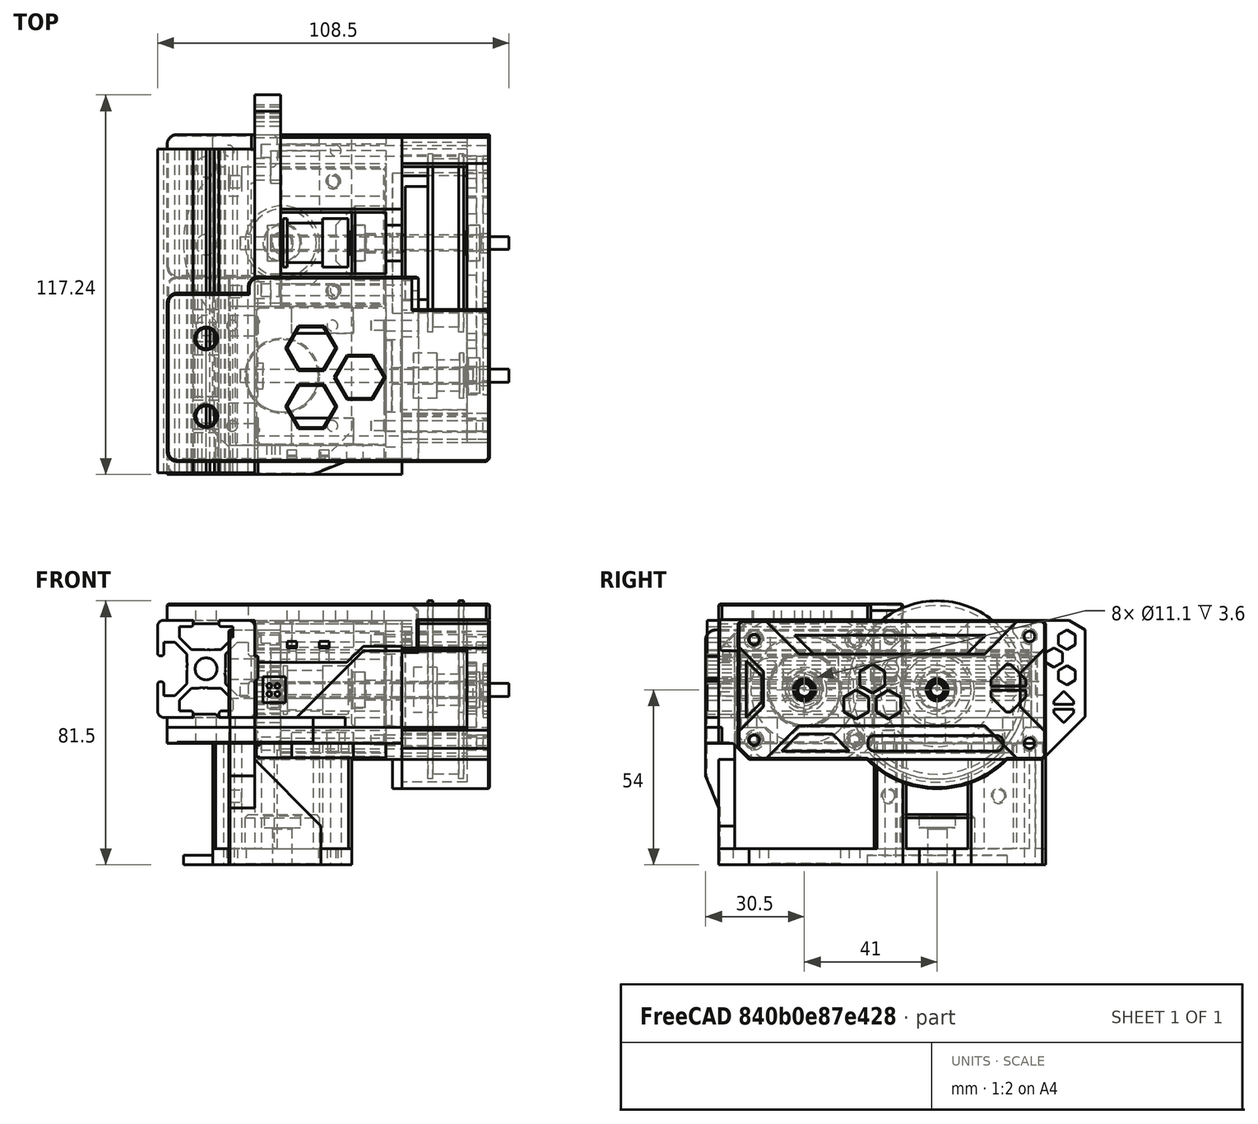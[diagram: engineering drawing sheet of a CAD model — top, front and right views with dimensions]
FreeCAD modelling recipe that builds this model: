
FCSTD DOCUMENT  (FreeCAD 0.19R24291 (Git))
Label: 80t-gearbox
License: Other
LicenseURL: GPL3
objects: Part::Box×56, Part::Chamfer×48, Part::Cylinder×46, Part::MultiFuse×43, Part::Cut×30, Part::Feature×25, Part::Fillet×5, Part::Refine×3, Part::MultiCommon×1
note: 257 computed .brp shape members not serialized (recipe doc carries the construction recipe); baked Part::Feature solids carry a one-line shape summary decoded from their .brp

FEATURE [Part::Feature] Cut001002  label="80t-pulley"
  Placement = pos=(64.5,41,8.5) rot=(0.707107,0,-0.707107;3.14159rad)
  shape: bbox 18 x 55 x 55 mm, 10 faces (baked)
FEATURE [Part::Feature] Cut001001  label="16t-pulley"
  Placement = pos=(64.5,0,8.5) rot=(0,-1,0;1.5708rad)
  shape: bbox 15.5 x 13.9 x 13.9 mm, 8 faces (baked)
FEATURE [Part::Feature] Fusion006002011004053036004001001  label="motor-40mm"
  Placement = pos=(0.5,0,8.5) rot=(0,1,0;1.5708rad)
  shape: bbox 67 x 47 x 42 mm, 100 faces (baked)
FEATURE [Part::Feature] Extrude001003002002002002  label="Extrude001003002002004"
  Placement = pos=(-15,-30,15) rot=(-1,0,0;1.5708rad)
  shape: bbox 30 x 100 x 30 mm, 95 faces (baked)
FEATURE [Part::Feature] Cut001  label="20t-pulley"
  Placement = pos=(8.8,41,8.5) rot=(0.707107,0,0.707107;3.14159rad)
  shape: bbox 20 x 15 x 15 mm, 8 faces (baked)
FEATURE [Part::Feature] Cut001003  label="MR115ZZ001"
  Placement = pos=(69.5,0,8.5) rot=(0,-1,0;1.5708rad)
  shape: bbox 4 x 11 x 11 mm, 4 faces (baked)
FEATURE [Part::Feature] Cut001004  label="MR115ZZ002"
  Placement = pos=(69.5,41,8.5) rot=(0,-1,0;1.5708rad)
  shape: bbox 4 x 11 x 11 mm, 4 faces (baked)
FEATURE [Part::Feature] Cut001005  label="MR115ZZ003"
  Placement = pos=(34,41,8.5) rot=(0,-1,0;1.5708rad)
  shape: bbox 4 x 11 x 11 mm, 4 faces (baked)
FEATURE [Part::Cylinder] Cylinder  label="POSA"
  Angle = 360
  AttacherType = Attacher::AttachEngine3D
  Height = 83
  Placement = pos=(-4.5,0,8.5) rot=(0,1,0;1.5708rad)
  Radius = 2
FEATURE [Part::Cylinder] Cylinder001  label="POSB"
  Angle = 360
  AttacherType = Attacher::AttachEngine3D
  Height = 83
  Placement = pos=(-4.5,41,8.5) rot=(0,1,0;1.5708rad)
  Radius = 2
FEATURE [Part::Box] Box  label="Cube"
  AttacherType = Attacher::AttachEngine3D
  Height = 43
  Length = 5
  Placement = pos=(40.5,-26.5,-13) rot=(0,0,1;0rad)
  Width = 101
FEATURE [Part::Box] Box001  label="Cube001"
  AttacherType = Attacher::AttachEngine3D
  Height = 43
  Length = 8
  Placement = pos=(0,21.5,-13) rot=(0,0,1;0rad)
  Width = 53
FEATURE [Part::Cylinder] Cylinder002  label="br01"
  Angle = 360
  AttacherType = Attacher::AttachEngine3D
  Height = 4
  Placement = pos=(4,41,8.5) rot=(0,1,0;1.5708rad)
  Radius = 5.55
FEATURE [Part::Cylinder] Cylinder003  label="br002"
  Angle = 360
  AttacherType = Attacher::AttachEngine3D
  Height = 4
  Placement = pos=(30,41,8.5) rot=(0,1,0;1.5708rad)
  Radius = 5.55
FEATURE [Part::Cylinder] Cylinder004  label="br003"
  Angle = 360
  AttacherType = Attacher::AttachEngine3D
  Height = 4
  Placement = pos=(65.5,41,8.5) rot=(0,1,0;1.5708rad)
  Radius = 5.55
FEATURE [Part::Cylinder] Cylinder005  label="br004"
  Angle = 360
  AttacherType = Attacher::AttachEngine3D
  Height = 4
  Placement = pos=(65.5,0,8.5) rot=(0,1,0;1.5708rad)
  Radius = 5.55
FEATURE [Part::Box] Box002  label="Cube002"
  AttacherType = Attacher::AttachEngine3D
  Height = 8
  Length = 27
  Placement = pos=(-27,30.5,-8) rot=(0,0,1;0rad)
  Width = 44
FEATURE [Part::Box] Box003  label="Cube003"
  AttacherType = Attacher::AttachEngine3D
  Height = 7.8
  Length = 1
  Placement = pos=(-1,29.5,11.1) rot=(0,0,1;0rad)
  Width = 32
FEATURE [Part::Feature] Cut001006  label="MR115ZZ004"
  Placement = pos=(8,41,8.5) rot=(0,-1,0;1.5708rad)
  shape: bbox 4 x 11 x 11 mm, 4 faces (baked)
FEATURE [Part::Cut] Cut
  Base = -> Box001
  Tool = -> Cylinder002
FEATURE [Part::Chamfer] Chamfer
  Base = -> Cut
  Edges = 1 edges r=0.4: [Edge13]
FEATURE [Part::Cylinder] Cylinder006  label="Cylinder"
  Angle = 360
  AttacherType = Attacher::AttachEngine3D
  Height = 10
  Placement = pos=(-3e-15,26.5,15) rot=(0,1,0;1.5708rad)
  Radius = 2.65
FEATURE [Part::Cylinder] Cylinder007  label="Cylinder001"
  Angle = 360
  AttacherType = Attacher::AttachEngine3D
  Height = 3
  Placement = pos=(5,26.5,15) rot=(0,1,0;1.5708rad)
  Radius = 5
FEATURE [Part::MultiFuse] Fusion
  Shapes = -> [Cylinder007,Cylinder006]
FEATURE [Part::Feature] Fusion006002011004053036004001002  label="Fusion001"
  Placement = pos=(0,38,0) rot=(0,0,1;0rad)
  shape: bbox 10 x 10 x 10 mm, 7 faces (baked)
FEATURE [Part::MultiFuse] Fusion006002011004053036004001003
  Shapes = -> [Fusion,Fusion006002011004053036004001002]
FEATURE [Part::Box] Box004  label="Cube004"
  AttacherType = Attacher::AttachEngine3D
  Height = 10
  Length = 3
  Placement = pos=(5,16.5,10) rot=(0,0,1;0rad)
  Width = 10
FEATURE [Part::MultiFuse] Fusion006002011004053036004001004
  Shapes = -> [Box004,Fusion006002011004053036004001003]
FEATURE [Part::Cut] Cut001007
  Base = -> Chamfer
  Tool = -> Fusion006002011004053036004001004
FEATURE [Part::Box] Box005  label="Cube005"
  AttacherType = Attacher::AttachEngine3D
  Height = 7.8
  Length = 1
  Placement = pos=(-1,67.5,11.1) rot=(0,0,1;0rad)
  Width = 7
FEATURE [Part::Box] Box006  label="Cube006"
  AttacherType = Attacher::AttachEngine3D
  Height = 13
  Length = 10
  Placement = pos=(-1.5,20.5,-13) rot=(0,0,1;0rad)
  Width = 10
FEATURE [Part::Cut] Cut001008
  Base = -> Cut001007
  Tool = -> Box006
FEATURE [Part::Chamfer] Chamfer001
  Base = -> Cut001008
  Edges = 1 edges r=5: [Edge30]
FEATURE [Part::Fillet] Fillet
  Base = -> Box002
  Edges = 2 edges r=3: [Edge1,Edge3]
FEATURE [Part::Box] Box007  label="Cube007"
  AttacherType = Attacher::AttachEngine3D
  Height = 28.5
  Length = 28
  Placement = pos=(13,-26.5,-8) rot=(0,0,1;0rad)
  Width = 5
FEATURE [Part::Box] Box009  label="Cube009"
  AttacherType = Attacher::AttachEngine3D
  Height = 8
  Length = 72
  Placement = pos=(-27,-26.5,-8) rot=(0,0,1;0rad)
  Width = 57
FEATURE [Part::Box] Box010  label="Cube010"
  AttacherType = Attacher::AttachEngine3D
  Height = 8
  Length = 40.5
  Placement = pos=(0,-21.5,-8) rot=(0,0,1;0rad)
  Width = 43
FEATURE [Part::Fillet] Fillet001
  Base = -> Box009
  Edges = 2 edges r=3: [Edge1,Edge3]
FEATURE [Part::Cut] Cut001009
  Base = -> Fillet001
  Tool = -> Box010
FEATURE [Part::Box] Box011  label="Cube011"
  AttacherType = Attacher::AttachEngine3D
  Height = 10
  Length = 33
  Placement = pos=(8,50.5,20) rot=(0,0,1;0rad)
  Width = 24
FEATURE [Part::Box] Box012  label="Cube012"
  AttacherType = Attacher::AttachEngine3D
  Height = 20
  Length = 33
  Placement = pos=(8,64.5,-13) rot=(0,0,1;0rad)
  Width = 10
FEATURE [Part::Box] Box013  label="Cube013"
  AttacherType = Attacher::AttachEngine3D
  Height = 10
  Length = 33
  Placement = pos=(8,21.5,20) rot=(0,0,1;0rad)
  Width = 10
FEATURE [Part::Chamfer] Chamfer002
  Base = -> Chamfer001
  Edges = 4 edges r=1: [Edge16,Edge19,Edge24,Edge25]
FEATURE [Part::Chamfer] Chamfer005
  Base = -> Box013
  Edges = 4 edges r=1: [Edge9,Edge10,Edge11,Edge12]
FEATURE [Part::Chamfer] Chamfer006
  Base = -> Chamfer002
  Edges = 2 edges r=1: [Edge39,Edge43]
FEATURE [Part::Box] Box014  label="Cube014"
  AttacherType = Attacher::AttachEngine3D
  Height = 10
  Length = 10
  Placement = pos=(-1,30.5,-18) rot=(0,0,1;0rad)
  Width = 35
FEATURE [Part::Chamfer] Chamfer007
  Base = -> Box014
  Edges = 1 edges r=5: [Edge12]
FEATURE [Part::Cut] Cut001010
  Base = -> Chamfer006
  Tool = -> Chamfer007
FEATURE [Part::Cylinder] Cylinder008  label="Cylinder002"
  Angle = 360
  AttacherType = Attacher::AttachEngine3D
  Height = 110
  Placement = pos=(2,26.5,25) rot=(0,1,0;1.5708rad)
  Radius = 1.65
FEATURE [Part::Cylinder] Cylinder009  label="Cylinder003"
  Angle = 360
  AttacherType = Attacher::AttachEngine3D
  Height = 110
  Placement = pos=(2,69.5,25) rot=(0,1,0;1.5708rad)
  Radius = 1.65
FEATURE [Part::Cylinder] Cylinder010  label="Cylinder004"
  Angle = 360
  AttacherType = Attacher::AttachEngine3D
  Height = 110
  Placement = pos=(2,69.5,-8) rot=(0,1,0;1.5708rad)
  Radius = 1.65
FEATURE [Part::Cylinder] Cylinder011  label="Cylinder005"
  Angle = 360
  AttacherType = Attacher::AttachEngine3D
  Height = 6
  Placement = pos=(2,69.5,-8) rot=(0,1,0;1.5708rad)
  Radius = 2
FEATURE [Part::Cylinder] Cylinder012  label="Cylinder006"
  Angle = 360
  AttacherType = Attacher::AttachEngine3D
  Height = 6
  Placement = pos=(2,69.5,25) rot=(0,1,0;1.5708rad)
  Radius = 2
FEATURE [Part::Cylinder] Cylinder013  label="Cylinder007"
  Angle = 360
  AttacherType = Attacher::AttachEngine3D
  Height = 6
  Placement = pos=(2,26.5,25) rot=(0,1,0;1.5708rad)
  Radius = 2
FEATURE [Part::MultiFuse] Fusion006002011004053036004001006
  Shapes = -> [Cylinder013,Cylinder012,Cylinder011]
FEATURE [Part::Cut] Cut001011
  Base = -> Cut001010
  Tool = -> Fusion006002011004053036004001006
FEATURE [Part::MultiFuse] Fusion006002011004053036004001007
  Shapes = -> [Cylinder010,Cylinder008,Cylinder009]
FEATURE [Part::Chamfer] Chamfer008
  Base = -> Box
  Edges = 2 edges r=1: [Edge11,Edge12]
FEATURE [Part::Chamfer] Chamfer009
  Base = -> Box011
  Edges = 4 edges r=1: [Edge9,Edge10,Edge11,Edge12]
FEATURE [Part::Cylinder] Cylinder014  label="Cylinder008"
  Angle = 360
  AttacherType = Attacher::AttachEngine3D
  Height = 10
  Placement = pos=(-15,40.5,0) rot=(0,0,1;0rad)
  Radius = 3.15
FEATURE [Part::Cylinder] Cylinder015  label="Cylinder009"
  Angle = 360
  AttacherType = Attacher::AttachEngine3D
  Height = 10
  Placement = pos=(-15,64.5,0) rot=(0,0,1;0rad)
  Radius = 3.15
FEATURE [Part::MultiFuse] Fusion006002011004053036004001009
  Placement = pos=(0,0,-10) rot=(0,0,1;0rad)
  Shapes = -> [Cylinder014,Cylinder015]
FEATURE [Part::Cut] Cut001012
  Base = -> Fillet
  Tool = -> Fusion006002011004053036004001009
FEATURE [Part::Chamfer] Chamfer011
  Base = -> Cut001012
  Edges = 5 edges r=0.4: [Edge4,Edge12,Edge14,Edge16,Edge17]
FEATURE [Part::Chamfer] Chamfer012
  Base = -> Cut001011
  Edges = 1 edges r=0.4: [Edge45]
FEATURE [Part::MultiFuse] Fusion006002011004053036004001010
  Shapes = -> [Box005,Box003]
FEATURE [Part::MultiFuse] Fusion006002011004053036004001011  label="back-plate"
  Shapes = -> [Chamfer012,Fusion006002011004053036004001010,Chamfer011]
FEATURE [Part::Box] Box015  label="Cube015"
  AttacherType = Attacher::AttachEngine3D
  Height = 10
  Length = 10
  Placement = pos=(36.5,17,-18) rot=(0,0,1;0rad)
  Width = 48.5
FEATURE [Part::Box] Box016  label="Cube016"
  AttacherType = Attacher::AttachEngine3D
  Height = 10
  Length = 10
  Placement = pos=(36.5,-75.5,-18) rot=(0,0,1;0rad)
  Width = 58.5
FEATURE [Part::Chamfer] Chamfer013
  Base = -> Box016
  Edges = 1 edges r=5: [Edge12]
FEATURE [Part::Cut] Cut001013
  Base = -> Chamfer008
  Tool = -> Chamfer013
FEATURE [Part::Chamfer] Chamfer014
  Base = -> Box015
  Edges = 2 edges r=5: [Edge10,Edge12]
FEATURE [Part::Cut] Cut001014
  Base = -> Cut001013
  Tool = -> Chamfer014
FEATURE [Part::Chamfer] Chamfer015
  Base = -> Cut001014
  Edges = 1 edges r=9.5: [Edge33]
FEATURE [Part::Chamfer] Chamfer016
  Base = -> Cut001009
  Edges = 5 edges r=0.4: [Edge4,Edge14,Edge16,Edge18,Edge19]
FEATURE [Part::Cylinder] Cylinder016  label="POSA001"
  Angle = 360
  AttacherType = Attacher::AttachEngine3D
  Height = 83
  Placement = pos=(2.5,0,8.5) rot=(0,1,0;1.5708rad)
  Radius = 11.15
FEATURE [Part::Chamfer] Chamfer017
  Base = -> Chamfer015
  Edges = 1 edges r=0.4: [Edge16]
FEATURE [Part::Cylinder] Cylinder017  label="Cylinder010"
  Angle = 360
  AttacherType = Attacher::AttachEngine3D
  Height = 10
  Placement = pos=(-15,15.5,0) rot=(0,0,1;0rad)
  Radius = 3.15
FEATURE [Part::Cylinder] Cylinder018  label="Cylinder011"
  Angle = 360
  AttacherType = Attacher::AttachEngine3D
  Height = 10
  Placement = pos=(-15,-11.5,0) rot=(0,0,1;0rad)
  Radius = 3.15
FEATURE [Part::MultiFuse] Fusion006002011004053036004001012
  Placement = pos=(0,0,-9) rot=(0,0,1;0rad)
  Shapes = -> [Cylinder017,Cylinder018]
FEATURE [Part::Cut] Cut001015
  Base = -> Chamfer016
  Tool = -> Fusion006002011004053036004001012
FEATURE [Part::Chamfer] Chamfer018
  Base = -> Box007
  Edges = 1 edges r=0.5: [Edge9]
FEATURE [Part::Chamfer] Chamfer019
  Base = -> Chamfer018
  Edges = 1 edges r=20.5: [Edge3]
FEATURE [Part::Box] Box017  label="Cube017"
  AttacherType = Attacher::AttachEngine3D
  Height = 2
  Length = 7.8
  Placement = pos=(-18.9,-26.5,0) rot=(0,0,1;0rad)
  Width = 11
FEATURE [Part::Box] Box018  label="Cube018"
  AttacherType = Attacher::AttachEngine3D
  Height = 2
  Length = 7.8
  Placement = pos=(-18.9,-7.5,0) rot=(0,0,1;0rad)
  Width = 19
FEATURE [Part::Box] Box019  label="Cube019"
  AttacherType = Attacher::AttachEngine3D
  Height = 2
  Length = 7.8
  Placement = pos=(-18.9,19.5,0) rot=(0,0,1;0rad)
  Width = 11
FEATURE [Part::MultiFuse] Fusion006002011004053036004001013
  Placement = pos=(0,0,-1) rot=(0,0,1;0rad)
  Shapes = -> [Box018,Box019,Box017]
FEATURE [Part::Chamfer] Chamfer020
  Base = -> Fusion006002011004053036004001013
  Edges = 3 edges r=1: [Edge6,Edge18,Edge30]
FEATURE [Part::MultiFuse] Fusion006002011004053036004001014
  Shapes = -> [Chamfer020,Cut001015]
FEATURE [Part::MultiFuse] Fusion006002011004053036004001015
  Shapes = -> [Fusion006002011004053036004001014,Chamfer019,Chamfer017]
FEATURE [Part::Cut] Cut001016
  Base = -> Fusion006002011004053036004001015
  Tool = -> Cylinder016
FEATURE [Part::Cylinder] Cylinder019  label="POSA002"
  Angle = 360
  AttacherType = Attacher::AttachEngine3D
  Height = 30
  Placement = pos=(32,15.5,24) rot=(0,1,0;1.5708rad)
  Radius = 1.65
FEATURE [Part::Cylinder] Cylinder020  label="POSA003"
  Angle = 360
  AttacherType = Attacher::AttachEngine3D
  Height = 30
  Placement = pos=(32,-15.5,24) rot=(0,1,0;1.5708rad)
  Radius = 1.65
FEATURE [Part::Cylinder] Cylinder021  label="POSA004"
  Angle = 360
  AttacherType = Attacher::AttachEngine3D
  Height = 30
  Placement = pos=(32,-15.5,-7) rot=(0,1,0;1.5708rad)
  Radius = 1.65
FEATURE [Part::Cylinder] Cylinder022  label="POSA005"
  Angle = 360
  AttacherType = Attacher::AttachEngine3D
  Height = 30
  Placement = pos=(32,15.5,-7) rot=(0,1,0;1.5708rad)
  Radius = 1.65
FEATURE [Part::MultiFuse] Fusion006002011004053036004001016
  Shapes = -> [Cylinder022,Cylinder021,Cylinder020,Cylinder019]
FEATURE [Part::Cut] Cut001017
  Base = -> Cut001016
  Tool = -> Fusion006002011004053036004001016
FEATURE [Part::Cylinder] Cylinder023  label="POSB001"
  Angle = 360
  AttacherType = Attacher::AttachEngine3D
  Height = 12
  Placement = pos=(30,41,8.5) rot=(0,1,0;1.5708rad)
  Radius = 11.5
FEATURE [Part::Chamfer] Chamfer021
  Base = -> Cylinder023
  Edges = 1 edges r=1: [Edge3]
FEATURE [Part::Cut] Cut001018
  Base = -> Chamfer021
  Tool = -> Cylinder003
FEATURE [Part::Chamfer] Chamfer022
  Base = -> Cut001018
  Edges = 1 edges r=0.4: [Edge6]
FEATURE [Part::Cylinder] Cylinder024  label="POSB002"
  Angle = 360
  AttacherType = Attacher::AttachEngine3D
  Height = 83
  Placement = pos=(-4.5,41,8.5) rot=(0,1,0;1.5708rad)
  Radius = 3
FEATURE [Part::Chamfer] Chamfer023
  Base = -> Box012
  Edges = 4 edges r=1: [Edge9,Edge10,Edge11,Edge12]
FEATURE [Part::MultiFuse] Fusion006002011004053036004001017
  Shapes = -> [Chamfer023,Chamfer009,Chamfer005]
FEATURE [Part::MultiFuse] Fusion006002011004053036004001018
  Shapes = -> [Cut001017,Chamfer022]
FEATURE [Part::Cut] Cut001019
  Base = -> Fusion006002011004053036004001018
  Tool = -> Cylinder024
FEATURE [Part::Chamfer] Chamfer024
  Base = -> Cut001019
  Edges = 3 edges r=0.4: [Edge126,Edge173,Edge202]
FEATURE [Part::MultiFuse] Fusion006002011004053036004001019
  Shapes = -> [Chamfer024,Fusion006002011004053036004001017]
FEATURE [Part::Box] Box020  label="Cube020"
  AttacherType = Attacher::AttachEngine3D
  Height = 10
  Length = 10
  Placement = pos=(38.5,30.5,35) rot=(0,0,1;0rad)
  Width = 21
FEATURE [Part::Chamfer] Chamfer025
  Base = -> Box020
  Edges = 2 edges r=5: [Edge9,Edge11]
  Placement = pos=(0,0,-10) rot=(0,0,1;0rad)
FEATURE [Part::Cut] Cut001020
  Base = -> Fusion006002011004053036004001019
  Tool = -> Fusion006002011004053036004001007
FEATURE [Part::Cut] Cut001021  label="z-motor-plate"
  Base = -> Cut001020
  Tool = -> Chamfer025
FEATURE [Part::Box] Box021  label="Cube021"
  AttacherType = Attacher::AttachEngine3D
  Height = 10
  Length = 5
  Placement = pos=(45.5,-26.5,20.5) rot=(0,0,1;0rad)
  Width = 57
FEATURE [Part::Box] Box022  label="Cube022"
  AttacherType = Attacher::AttachEngine3D
  Height = 9
  Length = 50.5
  Placement = pos=(0,-26.5,22) rot=(0,0,1;0rad)
  Width = 8
FEATURE [Part::Chamfer] Chamfer026
  Base = -> Box022
  Edges = 1 edges r=7: [Edge11]
FEATURE [Part::Box] Box023  label="Cube023"
  AttacherType = Attacher::AttachEngine3D
  Height = 5
  Length = 77.5
  Placement = pos=(-27,-26.5,30) rot=(0,0,1;0rad)
  Width = 57
FEATURE [Part::Chamfer] Chamfer027
  Base = -> Box021
  Edges = 2 edges r=1: [Edge9,Edge11]
FEATURE [Part::Cylinder] Cylinder025  label="POSA006"
  Angle = 360
  AttacherType = Attacher::AttachEngine3D
  Height = 83
  Placement = pos=(18.5,0,8.5) rot=(0,1,0;1.5708rad)
  Radius = 17
FEATURE [Part::Cut] Cut001022
  Base = -> Chamfer027
  Tool = -> Cylinder025
FEATURE [Part::Box] Box024  label="Cube024"
  AttacherType = Attacher::AttachEngine3D
  Height = 1
  Length = 7.8
  Placement = pos=(-18.9,-7.5,29) rot=(0,0,1;0rad)
  Width = 14
FEATURE [Part::Box] Box025  label="Cube025"
  AttacherType = Attacher::AttachEngine3D
  Height = 1
  Length = 7.8
  Placement = pos=(-18.9,-26.5,29) rot=(0,0,1;0rad)
  Width = 9
FEATURE [Part::Box] Box026  label="Cube026"
  AttacherType = Attacher::AttachEngine3D
  Height = 1
  Length = 7.8
  Placement = pos=(-18.9,16.5,29) rot=(0,0,1;0rad)
  Width = 9
FEATURE [Part::Cylinder] Cylinder026  label="Cylinder012"
  Angle = 360
  AttacherType = Attacher::AttachEngine3D
  Height = 10
  Placement = pos=(-15,11.5,26) rot=(0,0,1;0rad)
  Radius = 3.15
FEATURE [Part::Cylinder] Cylinder027  label="Cylinder013"
  Angle = 360
  AttacherType = Attacher::AttachEngine3D
  Height = 10
  Placement = pos=(-15,-12.5,26) rot=(0,0,1;0rad)
  Radius = 3.15
FEATURE [Part::Cylinder] Cylinder028  label="POSA007"
  Angle = 360
  AttacherType = Attacher::AttachEngine3D
  Height = 83
  Placement = pos=(25.5,-15.5,24) rot=(0,1,0;1.5708rad)
  Radius = 1.65
FEATURE [Part::Cylinder] Cylinder029  label="POSA008"
  Angle = 360
  AttacherType = Attacher::AttachEngine3D
  Height = 83
  Placement = pos=(25.5,15.5,24) rot=(0,1,0;1.5708rad)
  Radius = 1.65
FEATURE [Part::MultiFuse] Fusion006002011004053036004001024
  Shapes = -> [Cylinder029,Cylinder028]
FEATURE [Part::Box] Box027  label="Cube027"
  AttacherType = Attacher::AttachEngine3D
  Height = 10
  Length = 26
  Placement = pos=(45.5,64.5,-13) rot=(0,0,1;0rad)
  Width = 10
FEATURE [Part::Box] Box028  label="Cube028"
  AttacherType = Attacher::AttachEngine3D
  Height = 10
  Length = 26
  Placement = pos=(45.5,64.5,20) rot=(0,0,1;0rad)
  Width = 10
FEATURE [Part::Box] Box029  label="Cube029"
  AttacherType = Attacher::AttachEngine3D
  Height = 9.5
  Length = 21
  Placement = pos=(50.5,-20.5,20.5) rot=(0,0,1;0rad)
  Width = 10
FEATURE [Part::Box] Box030  label="Cube030"
  AttacherType = Attacher::AttachEngine3D
  Height = 10
  Length = 26
  Placement = pos=(45.5,-20.5,-13) rot=(0,0,1;0rad)
  Width = 10
FEATURE [Part::Cylinder] Cylinder030  label="POSB003"
  Angle = 360
  AttacherType = Attacher::AttachEngine3D
  Height = 83
  Placement = pos=(20.5,41,8.5) rot=(0,1,0;1.5708rad)
  Radius = 29.5
FEATURE [Part::Cylinder] Cylinder031  label="POSA009"
  Angle = 360
  AttacherType = Attacher::AttachEngine3D
  Height = 83
  Placement = pos=(-4.5,0,8.5) rot=(0,1,0;1.5708rad)
  Radius = 17
FEATURE [Part::MultiFuse] Fusion006002011004053036004001025
  Shapes = -> [Box030,Box029,Box027,Box028]
FEATURE [Part::Cut] Cut001024002
  Base = -> Fusion006002011004053036004001025
  Tool = -> Cylinder030
FEATURE [Part::Chamfer] Chamfer030
  Base = -> Cut001024002
  Edges = 1 edges r=3.5: [Edge9]
FEATURE [Part::Cut] Cut001024003
  Base = -> Chamfer030
  Tool = -> Cylinder031
FEATURE [Part::Chamfer] Chamfer031
  Base = -> Cut001024003
  Edges = 11 edges r=1: [Edge9,Edge15,Edge24,Edge26,Edge32,Edge41,Edge44,Edge46,Edge55,Edge57,Edge59]
FEATURE [Part::Box] Box032  label="Cube032"
  AttacherType = Attacher::AttachEngine3D
  Height = 43
  Length = 7
  Placement = pos=(65.5,-20.5,-13) rot=(0,0,1;0rad)
  Width = 95
FEATURE [Part::Chamfer] Chamfer032
  Base = -> Box032
  Edges = 1 edges r=3.5: [Edge9]
FEATURE [Part::Chamfer] Chamfer033
  Base = -> Chamfer032
  Edges = 3 edges r=1: [Edge8,Edge11,Edge13]
FEATURE [Part::Cylinder] Cylinder032  label="POSB004"
  Angle = 360
  AttacherType = Attacher::AttachEngine3D
  Height = 83
  Placement = pos=(-4.5,41,8.5) rot=(0,1,0;1.5708rad)
  Radius = 3
FEATURE [Part::Cylinder] Cylinder033  label="POSA010"
  Angle = 360
  AttacherType = Attacher::AttachEngine3D
  Height = 83
  Placement = pos=(-4.5,0,8.5) rot=(0,1,0;1.5708rad)
  Radius = 3
FEATURE [Part::MultiFuse] Fusion006002011004053036004001026
  Shapes = -> [Cylinder033,Cylinder032,Cylinder005,Cylinder004]
FEATURE [Part::Cut] Cut001024004
  Base = -> Chamfer033
  Tool = -> Fusion006002011004053036004001026
FEATURE [Part::Chamfer] Chamfer034
  Base = -> Cut001024004
  Edges = 4 edges r=0.4: [Edge9,Edge10,Edge31,Edge32]
FEATURE [Part::Feature] Fusion006002011004053036004001028001  label="dog-bone-plate"
  shape: bbox 27 x 95 x 43 mm, 76 faces (baked)
FEATURE [Part::Cylinder] Cylinder034  label="POSB005"
  Angle = 360
  AttacherType = Attacher::AttachEngine3D
  Height = 83
  Placement = pos=(-4.5,69.5,-8) rot=(0,1,0;1.5708rad)
  Radius = 1.65
FEATURE [Part::Cylinder] Cylinder035  label="POSA011"
  Angle = 360
  AttacherType = Attacher::AttachEngine3D
  Height = 83
  Placement = pos=(-4.5,-15.5,-7) rot=(0,1,0;1.5708rad)
  Radius = 1.65
FEATURE [Part::Cylinder] Cylinder036  label="POSB006"
  Angle = 360
  AttacherType = Attacher::AttachEngine3D
  Height = 83
  Placement = pos=(-4.5,69.5,25) rot=(0,1,0;1.5708rad)
  Radius = 1.65
FEATURE [Part::Cylinder] Cylinder037  label="POSA012"
  Angle = 360
  AttacherType = Attacher::AttachEngine3D
  Height = 83
  Placement = pos=(-4.5,-15.5,24) rot=(0,1,0;1.5708rad)
  Radius = 1.65
FEATURE [Part::MultiFuse] Fusion006002011004053036004001028003
  Shapes = -> [Cylinder037,Cylinder036,Cylinder035,Cylinder034]
FEATURE [Part::Feature] Fusion006002011004053036004001028003001  label="Fusion006002011004053036004001028004"
  shape: bbox 83 x 88.3 x 36.3 mm, 12 faces, 4 solids (baked)
FEATURE [Part::MultiFuse] Fusion006002011004053036004001028003002
  Shapes = -> [Chamfer034,Chamfer031]
FEATURE [Part::Cut] Cut001024006  label="face-plate-plain"
  Base = -> Fusion006002011004053036004001028003002
  Tool = -> Fusion006002011004053036004001028003001
FEATURE [Part::Feature] Cut001024007  label="5mm-washer001"
  Placement = pos=(65,0,8.5) rot=(0,1,0;1.5708rad)
  shape: bbox 0.5 x 6.9 x 6.9 mm, 4 faces (baked)
FEATURE [Part::Feature] Cut001024008  label="5mm-washer002"
  Placement = pos=(65,41,8.5) rot=(0,1,0;1.5708rad)
  shape: bbox 0.5 x 6.9 x 6.9 mm, 4 faces (baked)
FEATURE [Part::Feature] Cut001024009  label="5mm-washer003"
  Placement = pos=(8,41,8.5) rot=(0,1,0;1.5708rad)
  shape: bbox 0.5 x 6.9 x 6.9 mm, 4 faces (baked)
FEATURE [Part::Feature] Cut001024010  label="5mm-washer004"
  Placement = pos=(29,41,8.5) rot=(0,1,0;1.5708rad)
  shape: bbox 0.5 x 6.9 x 6.9 mm, 4 faces (baked)
FEATURE [Part::Box] Box033  label="Cube033"
  AttacherType = Attacher::AttachEngine3D
  Height = 43
  Length = 8
  Placement = pos=(0,72.5,-13) rot=(0,0,1;0rad)
  Width = 14.24
FEATURE [Part::Feature] Body001  label="hex-cut"
  Placement = pos=(-5e-15,81,24) rot=(0,1,0;1.5708rad)
  shape: bbox 10 x 5.196 x 6 mm, 8 faces (baked)
FEATURE [Part::Feature] Body002  label="hex-cut001"
  Placement = pos=(-3.8e-15,77,18.5) rot=(0,1,0;1.5708rad)
  shape: bbox 10 x 5.196 x 6 mm, 8 faces (baked)
FEATURE [Part::Feature] Body004  label="hex-cut003"
  Placement = pos=(-3e-15,81,13) rot=(0,1,0;1.5708rad)
  shape: bbox 10 x 5.196 x 6 mm, 8 faces (baked)
FEATURE [Part::Box] Box034  label="Cube034"
  AttacherType = Attacher::AttachEngine3D
  Height = 4
  Length = 10
  Placement = pos=(0,77,4) rot=(0,0,1;0rad)
  Width = 6
FEATURE [Part::Box] Box035  label="Cube035"
  AttacherType = Attacher::AttachEngine3D
  Height = 4
  Length = 10
  Placement = pos=(0,77,-1.5) rot=(0,0,1;0rad)
  Width = 6
FEATURE [Part::MultiFuse] Fusion006002011004053036004001028003003
  Shapes = -> [Box035,Box034]
FEATURE [Part::Chamfer] Chamfer037
  Base = -> Fusion006002011004053036004001028003003
  Edges = 4 edges r=2.9: [Edge9,Edge11,Edge22,Edge24]
FEATURE [Part::MultiFuse] Fusion006002011004053036004001028003004
  Placement = pos=(0,0.1,0) rot=(0,0,1;0rad)
  Shapes = -> [Chamfer037,Body004,Body002,Body001]
FEATURE [Part::Cylinder] Cylinder038  label="5x65-shaft"
  Angle = 360
  AttacherType = Attacher::AttachEngine3D
  Height = 65
  Placement = pos=(5,41,8.5) rot=(0,1,0;1.5708rad)
  Radius = 2.5
FEATURE [Part::Box] Box036  label="Cube036"
  AttacherType = Attacher::AttachEngine3D
  Height = 10
  Length = 28
  Placement = pos=(-30,25.5,25) rot=(0,0,1;0rad)
  Width = 14
FEATURE [Part::Cut] Cut001024012
  Base = -> Box023
  Tool = -> Box036
FEATURE [Part::Fillet] Fillet002
  Base = -> Cut001024012
  Edges = 3 edges r=3: [Edge2,Edge4,Edge17]
FEATURE [Part::MultiFuse] Fusion006002011004053036004001028003008
  Shapes = -> [Cylinder027,Cylinder026]
FEATURE [Part::Feature] Fusion005
  Placement = pos=(7.5,-8.5,27) rot=(0,0,1;0rad)
  shape: bbox 30 x 30.99 x 10 mm, 24 faces, 3 solids (baked)
FEATURE [Part::Box] Box037  label="Cube037"
  AttacherType = Attacher::AttachEngine3D
  Height = 10
  Length = 14
  Placement = pos=(-6,-21.5,-10) rot=(0,0,1;0rad)
  Width = 43
FEATURE [Part::Fillet] Fillet003
  Base = -> Box037
  Edges = 2 edges r=1: [Edge1,Edge3]
FEATURE [Part::Box] Box038  label="Cube038"
  AttacherType = Attacher::AttachEngine3D
  Height = 5
  Length = 3
  Placement = pos=(45.5,23.5,20) rot=(0,0,1;0rad)
  Width = 6
FEATURE [Part::Cylinder] Cylinder039
  Angle = 360
  AttacherType = Attacher::AttachEngine3D
  Height = 3
  Placement = pos=(45.5,26.5,25) rot=(0,1,0;1.5708rad)
  Radius = 3
FEATURE [Part::MultiFuse] Fusion006002011004053036004001028003009
  Shapes = -> [Cylinder039,Box038]
FEATURE [Part::Feature] Cut001003001  label="80-t-mellow"
  Placement = pos=(64.5,41,8.5) rot=(0,-1,0;1.5708rad)
  shape: bbox 18 x 55 x 55 mm, 10 faces (baked)
FEATURE [Part::Cylinder] Cylinder040
  Angle = 360
  AttacherType = Attacher::AttachEngine3D
  Height = 28
  Placement = pos=(40,41,8.5) rot=(0,1,0;1.5708rad)
  Radius = 19
FEATURE [Part::Box] Box039  label="Cube039"
  AttacherType = Attacher::AttachEngine3D
  Height = 4.75
  Length = 24
  Placement = pos=(48.5,-26.5,30.25) rot=(0,0,1;0rad)
  Width = 47
FEATURE [Part::Chamfer] Chamfer029006004
  Base = -> Box039
  Edges = 2 edges r=1: [Edge5,Edge7]
FEATURE [Part::Cut] Cut001024014003001002006002  label="dog-bone-plate001"
  Base = -> Fusion006002011004053036004001028001
  Tool = -> Fusion006002011004053036004001028003
FEATURE [Part::Box] Box047  label="Cube047"
  AttacherType = Attacher::AttachEngine3D
  Height = 15
  Length = 33
  Placement = pos=(8,69.5,6) rot=(0,0,1;0rad)
  Width = 2
FEATURE [Part::Box] Box048  label="Cube048"
  AttacherType = Attacher::AttachEngine3D
  Height = 4
  Length = 33
  Placement = pos=(8,55.5,-8) rot=(0,0,1;0rad)
  Width = 9
FEATURE [Part::Cylinder] Cylinder042
  Angle = 360
  AttacherType = Attacher::AttachEngine3D
  Height = 10
  Placement = pos=(24.25,26,-14) rot=(0,0,1;0rad)
  Radius = 1.9
FEATURE [Part::Cut] Cut001024014003001002006003
  Base = -> Cut001021
  Tool = -> Fillet003
FEATURE [Part::Cylinder] Cylinder043
  Angle = 360
  AttacherType = Attacher::AttachEngine3D
  Height = 10
  Placement = pos=(24.25,26,-13) rot=(0,0,1;0rad)
  Radius = 1.65
FEATURE [Part::Cylinder] Cylinder044
  Angle = 360
  AttacherType = Attacher::AttachEngine3D
  Height = 10
  Placement = pos=(24.25,60,-13) rot=(0,0,1;0rad)
  Radius = 1.65
FEATURE [Part::Box] Box049  label="Cube049"
  AttacherType = Attacher::AttachEngine3D
  Height = 3
  Length = 32.25
  Placement = pos=(8,21.75,-11) rot=(0,0,1;0rad)
  Width = 42.5
FEATURE [Part::MultiFuse] Fusion006002011004053036004001028003011011
  Shapes = -> [Box048,Box047]
FEATURE [Part::Cylinder] Cylinder048
  Angle = 360
  AttacherType = Attacher::AttachEngine3D
  Height = 10
  Placement = pos=(24.25,60,-13) rot=(0,0,1;0rad)
  Radius = 1.9
FEATURE [Part::Box] Box060  label="Cube060"
  AttacherType = Attacher::AttachEngine3D
  Height = 6
  Length = 5
  Placement = pos=(40.5,16.5,-13) rot=(0,0,1;0rad)
  Width = 49.5
FEATURE [Part::Chamfer] Chamfer029006005010
  Base = -> Box060
  Edges = 2 edges r=3: [Edge10,Edge12]
FEATURE [Part::MultiFuse] Fusion006002011004053036004001028003011012
  Shapes = -> [Cut001024014003001002006003,Fusion006002011004053036004001028003011011,Chamfer029006005010]
FEATURE [Part::MultiFuse] Fusion006002011004053036004001028003011014
  Shapes = -> [Cylinder044,Cylinder043]
FEATURE [Part::Cylinder] Cylinder045
  Angle = 360
  AttacherType = Attacher::AttachEngine3D
  Height = 3
  Placement = pos=(42.5,41,8.5) rot=(0,1,0;1.5708rad)
  Radius = 30.5
FEATURE [Part::Box] Box061  label="Cube061"
  AttacherType = Attacher::AttachEngine3D
  Height = 10
  Length = 10
  Placement = pos=(35.5,8.5,-22.5) rot=(0,0,1;0rad)
  Width = 58
FEATURE [Part::Cut] Cut001024014003001002006005007
  Base = -> Box049
  Tool = -> Fusion006002011004053036004001028003011014
FEATURE [Part::Chamfer] Chamfer029006005013  label="bottom-cover-r1"
  Base = -> Cut001024014003001002006005007
  Edges = 6 edges r=0.4: [Edge4,Edge5,Edge12,Edge14,Edge15,Edge16]
FEATURE [Part::Feature] Fusion007001001  label="face-plate-type1-r003"
  Placement = pos=(72.5,27.5,8.5) rot=(0.57735,-0.57735,-0.57735;2.0944rad)
  shape: bbox 27 x 95 x 52 mm, 216 faces (baked)
FEATURE [Part::MultiCommon] Common
  Shapes = -> [Cylinder045,Box061]
FEATURE [Part::MultiFuse] Fusion006002011004053036004001028003011015
  Shapes = -> [Cylinder042,Cylinder048]
FEATURE [Part::Cut] Cut001024014003001002006005008
  Base = -> Fusion006002011004053036004001028003011012
  Tool = -> Fusion006002011004053036004001028003011015
FEATURE [Part::Chamfer] Chamfer029006005014
  Base = -> Cut001024014003001002006005008
  Edges = 2 edges r=0.4: [Edge246,Edge290]
FEATURE [Part::MultiFuse] Fusion006002011004053036004001028003011016  label="motor-plate-r3-up"
  Shapes = -> [Common,Chamfer029006005014]
FEATURE [Part::Refine] Chamfer029006005013001  label="bottom-cover-r002"
  Source = -> Chamfer029006005013
FEATURE [Part::Refine] Fusion007001001001  label="face-plate-type1-r004"
  Source = -> Fusion007001001
FEATURE [Part::Box] Box062  label="Cube062"
  AttacherType = Attacher::AttachEngine3D
  Height = 10
  Length = 33.5
  Placement = pos=(0,-26.5,17) rot=(0,0,1;0rad)
  Width = 5
FEATURE [Part::Chamfer] Chamfer029006005013002
  Base = -> Box062
  Edges = 1 edges r=5: [Edge8]
FEATURE [Part::Chamfer] Chamfer029006005013003
  Base = -> Chamfer029006005013002
  Edges = 1 edges r=1: [Edge15]
FEATURE [Part::Feature] Chamfer029006005013005001
  Placement = pos=(10,70,10.5) rot=(0,0,1;0rad)
  shape: bbox 3 x 10 x 11 mm, 13 faces (baked)
FEATURE [Part::Feature] Chamfer029006005013005002
  Placement = pos=(20,70,10.5) rot=(0,0,1;0rad)
  shape: bbox 3 x 10 x 11 mm, 13 faces (baked)
FEATURE [Part::MultiFuse] Fusion006002011004053036004001028003011016002
  Placement = pos=(0,0,2) rot=(0,0,1;0rad)
  Shapes = -> [Chamfer029006005013005001,Chamfer029006005013005002]
FEATURE [Part::Box] Box063  label="Cube063"
  AttacherType = Attacher::AttachEngine3D
  Height = 5
  Length = 7
  Placement = pos=(33,-26.5,22) rot=(0,0,1;0rad)
  Width = 5
FEATURE [Part::MultiFuse] Fusion006002011004053036004001028003011016003
  Shapes = -> [Chamfer029006005013003,Box063]
FEATURE [Part::Chamfer] Chamfer029006005013005004
  Base = -> Chamfer029006004
  Edges = 5 edges r=0.4: [Edge1,Edge5,Edge7,Edge8,Edge9]
FEATURE [Part::Box] Box064  label="Cube064"
  AttacherType = Attacher::AttachEngine3D
  Height = 21.5
  Length = 33
  Placement = pos=(8,21.5,0) rot=(0,0,1;0rad)
  Width = 7
FEATURE [Part::Box] Box066  label="Cube066"
  AttacherType = Attacher::AttachEngine3D
  Height = 3
  Length = 33
  Placement = pos=(8,27.5,-1) rot=(0,0,1;0rad)
  Width = 3
FEATURE [Part::Box] Box067  label="Cube067"
  AttacherType = Attacher::AttachEngine3D
  Height = 3
  Length = 33
  Placement = pos=(8,27.5,18) rot=(0,0,1;0rad)
  Width = 3
FEATURE [Part::Chamfer] Chamfer029006005013005005001002
  Base = -> Box067
  Edges = 1 edges r=2: [Edge11]
FEATURE [Part::Chamfer] Chamfer029006005013005005001003
  Base = -> Box066
  Edges = 1 edges r=2: [Edge12]
FEATURE [Part::MultiFuse] Fusion006002011004053036004001028003011016005  label="rf-1-motor"
  Shapes = -> [Chamfer029006005013005005001003,Box064,Chamfer029006005013005005001002]
FEATURE [Part::Box] Box068  label="Cube068"
  AttacherType = Attacher::AttachEngine3D
  Height = 5
  Length = 72.5
  Placement = pos=(-27,-30.5,-8) rot=(0,0,1;0rad)
  Width = 5
FEATURE [Part::Box] Box069  label="Cube069"
  AttacherType = Attacher::AttachEngine3D
  Height = 8
  Length = 55
  Placement = pos=(-27,-30.5,-8) rot=(0,0,1;0rad)
  Width = 5
FEATURE [Part::Chamfer] Chamfer029006005013005005001004
  Base = -> Box069
  Edges = 1 edges: [Edge5 r1=4 r2=10]
FEATURE [Part::Box] Box070  label="Cube070"
  AttacherType = Attacher::AttachEngine3D
  Height = 8
  Length = 6
  Placement = pos=(-27,-30.5,-8) rot=(0,0,1;0rad)
  Width = 8
FEATURE [Part::MultiFuse] Fusion006002011004053036004001028003011016006
  Shapes = -> [Chamfer029006005013005005001004,Box070]
FEATURE [Part::Box] Box071  label="Cube071"
  AttacherType = Attacher::AttachEngine3D
  Height = 1
  Length = 7.8
  Placement = pos=(-18.9,-30.5,0) rot=(0,0,1;0rad)
  Width = 8
FEATURE [Part::Chamfer] Chamfer029006005013005005001005
  Base = -> Box071
  Edges = 1 edges r=0.99: [Edge6]
FEATURE [Part::MultiFuse] Fusion006002011004053036004001028003011016007  label="rf-2-motor-base"
  Shapes = -> [Chamfer029006005013005005001005,Fusion006002011004053036004001028003011016006]
FEATURE [Part::Refine] Fusion006002011004053036004001028003011016007001  label="rf-2-motor-base001"
  Source = -> Fusion006002011004053036004001028003011016007
FEATURE [Part::Fillet] Fillet004
  Base = -> Fusion006002011004053036004001028003011016007001
  Edges = 1 edges r=3: [Edge37]
FEATURE [Part::Chamfer] Chamfer029006005013005005001006
  Base = -> Fillet004
  Edges = 5 edges r=0.4: [Edge3,Edge16,Edge21,Edge25,Edge26]
FEATURE [Part::MultiFuse] Fusion006002011004053036004001028003011016007002  label="motor-plate-r4"
  Shapes = -> [Fusion006002011004053036004001028003011016,Fusion006002011004053036004001028003011016005,Chamfer029006005013005005001006]
FEATURE [Part::Chamfer] Chamfer029006005013005005001007
  Base = -> Box033
  Edges = 1 edges: [Edge12 r1=3 r2=5]
FEATURE [Part::Chamfer] Chamfer029006005013005005001008
  Base = -> Chamfer029006005013005005001007
  Edges = 1 edges r=13.24: [Edge14]
FEATURE [Part::MultiFuse] Fusion006002011004053036004001028003011016007002001002
  Shapes = -> [Chamfer029006005013005005001008,Fusion006002011004053036004001011]
FEATURE [Part::Cut] Cut001024014003001002006005011
  Base = -> Fusion006002011004053036004001028003011016007002001002
  Tool = -> Fusion006002011004053036004001028003004
FEATURE [Part::Box] Box072  label="Cube072"
  AttacherType = Attacher::AttachEngine3D
  Height = 10
  Length = 10
  Placement = pos=(-10,21.5,10) rot=(0,0,1;0rad)
  Width = 10
FEATURE [Part::Box] Box073  label="Cube073"
  AttacherType = Attacher::AttachEngine3D
  Height = 10
  Length = 10
  Placement = pos=(-10,59.5,10) rot=(0,0,1;0rad)
  Width = 10
FEATURE [Part::MultiFuse] Fusion006002011004053036004001028003011016007002001003
  Shapes = -> [Box073,Box072]
FEATURE [Part::Chamfer] Chamfer029006005013005005001009
  Base = -> Cut001024014003001002006005011
  Edges = 3 edges r=0.4: [Edge178,Edge180,Edge182]
FEATURE [Part::Cut] Cut001024014003001002006005012  label="back-plate-f2"
  Base = -> Chamfer029006005013005005001009
  Refine = true
  Tool = -> Fusion006002011004053036004001028003011016007002001003
FEATURE [Part::Box] Box074  label="Cube074"
  AttacherType = Attacher::AttachEngine3D
  Height = 10
  Length = 10
  Placement = pos=(-20,10.5,0) rot=(0,0,1;0rad)
  Width = 10
FEATURE [Part::Box] Box075  label="Cube075"
  AttacherType = Attacher::AttachEngine3D
  Height = 10
  Length = 10
  Placement = pos=(-20,-16.5,0) rot=(0,0,1;0rad)
  Width = 10
FEATURE [Part::MultiFuse] Fusion006002011004053036004001028003011016007002001004
  Shapes = -> [Box074,Box075]
FEATURE [Part::Cut] Cut001024014003001002006005013  label="motor-plate-r5"
  Base = -> Fusion006002011004053036004001028003011016007002
  Refine = true
  Tool = -> Fusion006002011004053036004001028003011016007002001004
FEATURE [Part::Feature] Cut001024014003001002006005013001  label="z-motor-body-right"
  Placement = pos=(0,0,0) rot=(0,1,0;1.5708rad)
  shape: bbox 52 x 105 x 72.5 mm, 105 faces (baked)
FEATURE [Part::MultiFuse] Fusion006002011004053036004001028003011016007002001005
  Shapes = -> [Box026,Box024,Box025]
FEATURE [Part::Chamfer] Chamfer029006005013005005001010
  Base = -> Fillet002
  Edges = 1 edges r=2: [Edge9]
FEATURE [Part::MultiFuse] Fusion006002011004053036004001028003011016007002001008
  Refine = true
  Shapes = -> [Fusion006002011004053036004001028003011016003,Chamfer026,Chamfer029006005013005005001010,Fusion006002011004053036004001028003011016007002001005,Cut001022]
FEATURE [Part::MultiFuse] Fusion006002011004053036004001028003011016007002001009
  Refine = true
  Shapes = -> [Fusion006002011004053036004001028003008,Fusion005,Fusion006002011004053036004001028003011016002,Fusion006002011004053036004001024,Cylinder040,Fusion006002011004053036004001028003009]
FEATURE [Part::Cut] Cut001024014003001002006005013002
  Base = -> Fusion006002011004053036004001028003011016007002001008
  Tool = -> Fusion006002011004053036004001028003011016007002001009
FEATURE [Part::Chamfer] Chamfer029006005013005005001011
  Base = -> Cut001024014003001002006005013002
  Edges = 33 edges r=0.4: [Edge41,Edge44,Edge105,Edge106,Edge107,Edge115,Edge121,Edge136,Edge137,Edge138,Edge139,Edge140,Edge141,Edge142,Edge143,Edge144,Edge145,Edge146,Edge147,Edge148,Edge149,Edge150,Edge151,Edge152,Edge153,Edge154,Edge155,Edge156,Edge157,Edge158,Edge159,Edge160,Edge161]
FEATURE [Part::MultiFuse] Fusion006002011004053036004001028003011016007002001010  label="z-motor-top-plate-r5"
  Refine = true
  Shapes = -> [Chamfer029006005013005005001011,Chamfer029006005013005004]
